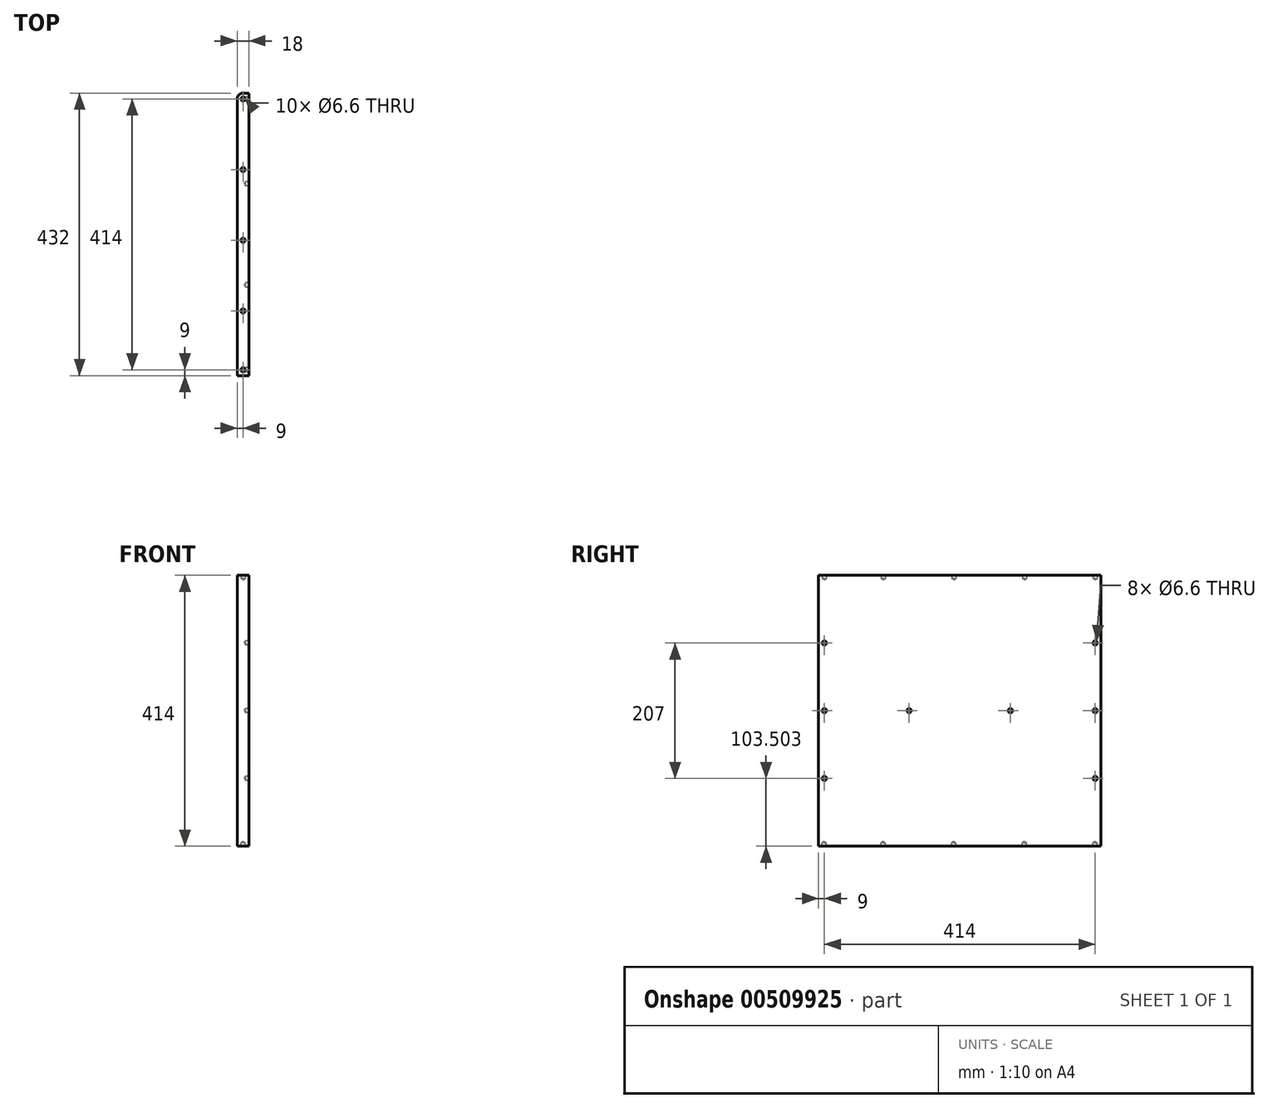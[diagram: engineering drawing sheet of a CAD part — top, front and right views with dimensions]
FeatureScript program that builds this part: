
annotation { "Feature Type Name" : "Feature", "Feature Type Description" : "" }
export const myFeature = defineFeature(function(context is Context, id is Id, definition is map)
    precondition{}
    {
        {
            var Q0;
            Q0=qCreatedBy(makeId("Front.planeOp"),FACE);
            var sketch = newSketch(context, id + "F0", { "sketchPlane" : qUnion([Q0])});
            skLineSegment(sketch, "E0", {"start": v(0, 199.43) * mm, "end": v(0, -214.57) * mm});
            skLineSegment(sketch, "E1", {"start": v(18, 199.43) * mm, "end": v(18, -214.57) * mm});
            skLineSegment(sketch, "E2", {"start": v(0, 199.43) * mm, "end": v(18, 199.43) * mm});
            skLineSegment(sketch, "E3", {"start": v(0, -214.57) * mm, "end": v(18, -214.57) * mm});
            skSolve(sketch);
        }
        {
            var Q0;
            Q0=qSketchRegion(id+"F0",true);
            extrude(context, id + "F1", {"entities" : qUnion([Q0]), "depth" : 432 * mm});
        }
        {
            var Q0;
            Q0=makeQuery(id+"F1.opExtrude","CAP_EDGE",EDGE,{"disambiguationData":[OSD([sQuery(id+"F0.wireOp",EDGE,"E1")])],"isStart":true});
            fillet(context, id + "F2", {"entities" : qUnion([Q0]), "radius" : 9 * mm, "tangentPropagation" : true, "allowEdgeOverflow" : false});
        }
        {
            var Q0;
            Q0=makeQuery(id+"F1.opExtrude","SWEPT_FACE",FACE,{"disambiguationData":[OSD([sQuery(id+"F0.wireOp",EDGE,"E0")])]});
            var sketch = newSketch(context, id + "F3", { "sketchPlane" : qUnion([Q0])});
            skLineSegment(sketch, "E4", {"start": v(9, -214.57) * mm, "end": v(9, 199.43) * mm});
            skLineSegment(sketch, "E5", {"start": v(423, -214.57) * mm, "end": v(423, 199.43) * mm});
            skPoint(sketch, "E6", {"position": v(9, -7.57) * mm});
            skPoint(sketch, "E7", {"position": v(423, -7.57) * mm});
            skLineSegment(sketch, "E8", {"start": v(9, -7.57) * mm, "end": v(9, 199.43) * mm});
            skLineSegment(sketch, "E9", {"start": v(423, 199.43) * mm, "end": v(423, -7.57) * mm});
            skLineSegment(sketch, "E10", {"start": v(423, -7.57) * mm, "end": v(423, -214.57) * mm});
            skLineSegment(sketch, "E11", {"start": v(9, -214.57) * mm, "end": v(9, -7.57) * mm});
            skPoint(sketch, "E12", {"position": v(9, 95.93) * mm});
            skPoint(sketch, "E13", {"position": v(423, 95.93) * mm});
            skPoint(sketch, "E14", {"position": v(423, -111.07) * mm});
            skPoint(sketch, "E15", {"position": v(9, -111.07) * mm});
            skLineSegment(sketch, "E16", {"start": v(432, -7.57) * mm, "end": v(0, -7.57) * mm});
            skPoint(sketch, "E17", {"position": v(293.4, -7.57) * mm});
            skPoint(sketch, "E18", {"position": v(138.6, -7.57) * mm});
            skSolve(sketch);
        }
        {
            var Q0;
            Q0=makeQuery(id+"F1.opExtrude","SWEPT_FACE",FACE,{"disambiguationData":[OSD([sQuery(id+"F0.wireOp",EDGE,"E3")])]});
            var sketch = newSketch(context, id + "F4", { "sketchPlane" : qUnion([Q0])});
            skLineSegment(sketch, "E19", {"start": v(9, 9) * mm, "end": v(9, 441) * mm});
            skPoint(sketch, "E19.endSnap0", {"position": v(9, 432) * mm});
            skPoint(sketch, "E20", {"position": v(9, 225) * mm});
            skLineSegment(sketch, "E21", {"start": v(9, 225) * mm, "end": v(9, 9) * mm});
            skLineSegment(sketch, "E22", {"start": v(9, 225) * mm, "end": v(9, 441) * mm});
            skPoint(sketch, "E23", {"position": v(9, 117) * mm});
            skPoint(sketch, "E24", {"position": v(9, 333) * mm});
            skPoint(sketch, "E25", {"position": v(9, 423) * mm});
            skSolve(sketch);
        }
        {
            var Q0;
            Q0=makeQuery(id+"F1.opExtrude","SWEPT_FACE",FACE,{"disambiguationData":[OSD([sQuery(id+"F0.wireOp",EDGE,"E2")])]});
            var sketch = newSketch(context, id + "F5", { "sketchPlane" : qUnion([Q0])});
            skLineSegment(sketch, "E26", {"start": v(9, -9) * mm, "end": v(9, -441) * mm});
            skPoint(sketch, "E26.endSnap0", {"position": v(9, -432) * mm});
            skPoint(sketch, "E27", {"position": v(9, -225) * mm});
            skLineSegment(sketch, "E28", {"start": v(9, -9) * mm, "end": v(9, -225) * mm});
            skLineSegment(sketch, "E29", {"start": v(9, -225) * mm, "end": v(9, -441) * mm});
            skLineSegment(sketch, "E30", {"start": v(9, -225) * mm, "end": v(9, -9) * mm});
            skPoint(sketch, "E31", {"position": v(9, -333) * mm});
            skPoint(sketch, "E32", {"position": v(9, -117) * mm});
            skPoint(sketch, "E33", {"position": v(9, -423) * mm});
            skSolve(sketch);
        }
        {
            var Q0;
            Q0=sQuery(id+"F4.wireOp",VERTEX,"E19.start");
            var Q1;
            Q1=sQuery(id+"F4.wireOp",VERTEX,"E23");
            var Q2;
            Q2=sQuery(id+"F4.wireOp",VERTEX,"E20");
            var Q3;
            Q3=sQuery(id+"F4.wireOp",VERTEX,"E24");
            var Q4;
            Q4=sQuery(id+"F4.wireOp",VERTEX,"E25");
            var Q5;
            Q5=sQuery(id+"F3.wireOp",VERTEX,"E14");
            var Q6;
            Q6=sQuery(id+"F3.wireOp",VERTEX,"E7");
            var Q7;
            Q7=sQuery(id+"F3.wireOp",VERTEX,"E13");
            var Q8;
            Q8=sQuery(id+"F3.wireOp",VERTEX,"E15");
            var Q9;
            Q9=sQuery(id+"F3.wireOp",VERTEX,"E11.end");
            var Q10;
            Q10=sQuery(id+"F3.wireOp",VERTEX,"E12");
            var Q11;
            Q11=sQuery(id+"F5.wireOp",VERTEX,"E32");
            var Q12;
            Q12=sQuery(id+"F5.wireOp",VERTEX,"E27");
            var Q13;
            Q13=sQuery(id+"F5.wireOp",VERTEX,"E31");
            var Q14;
            Q14=sQuery(id+"F5.wireOp",VERTEX,"E30.end");
            var Q15;
            Q15=sQuery(id+"F5.wireOp",VERTEX,"E33");
            var Q16;
            Q16=sQuery(id+"F3.wireOp",VERTEX,"17865de5-3030-4e56-9e9c-618e6b153631");
            var Q17;
            Q17=sQuery(id+"F3.wireOp",VERTEX,"e1923606-e960-492c-848d-222f9f50b01c");
            var Q18;
            Q18=sQuery(id+"F3.wireOp",VERTEX,"E18");
            var Q19;
            Q19=sQuery(id+"F3.wireOp",VERTEX,"E17");
            var Q20;
            Q20=makeQuery(id+"F1.opExtrude","SWEPT_BODY",BODY,{"disambiguationData":[OSD([sQuery(id+"F0.wireOp",EDGE,"E0"),sQuery(id+"F0.wireOp",EDGE,"E1"),sQuery(id+"F0.wireOp",EDGE,"E2"),sQuery(id+"F0.wireOp",EDGE,"E3")])]});
            hole(context, id + "F6", {"style" : HoleStyle.SIMPLE, "endStyle" : HoleEndStyle.BLIND, "standardTappedOrClearance" : lookupTablePath({ "standard" : "ISO", "fit" : "Normal", "size" : "M6", "type" : "Clearance" }), "standardBlindInLast" : lookupTablePath({ "fit" : "Standard", "standard" : "ISO", "size" : "M6", "type" : "Clearance" }), "holeDiameter" : 6.6 * mm, "holeDepth" : 5 * mm, "isTappedThrough" : true, "tappedDepth" : 12 * mm, "tapClearance" : 3, "locations" : qUnion([Q0, Q1, Q2, Q3, Q4, Q5, Q6, Q7, Q8, Q9, Q10, Q11, Q12, Q13, Q14, Q15, Q16, Q17, Q18, Q19]), "scope" : qUnion([Q20])});
        }
        {
            var Q0;
            Q0=makeQuery(id+"F1.opExtrude","SWEPT_BODY",BODY,{"disambiguationData":[OSD([sQuery(id+"F0.wireOp",EDGE,"E0"),sQuery(id+"F0.wireOp",EDGE,"E1"),sQuery(id+"F0.wireOp",EDGE,"E2"),sQuery(id+"F0.wireOp",EDGE,"E3")])]});
            var Q1;
            Q1=makeQuery(id+"F1.opExtrude","SWEPT_EDGE",EDGE,{"disambiguationData":[OSD([sQuery(id+"F0.wireOp",EDGE,"E0"),sQuery(id+"F0.wireOp",EDGE,"E2")])]});
            transform(context, id + "F7", {"entities" : qUnion([Q0]), "transformType" : TransformType.ROTATION, "transformAxis" : qUnion([Q1]), "angle" : 180 * degree, "makeCopy" : false});
        }
    });
